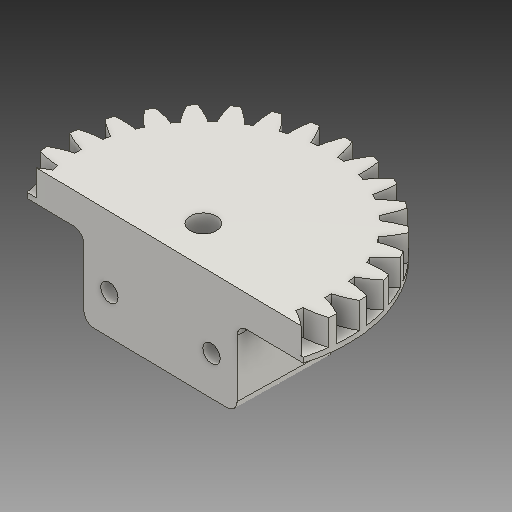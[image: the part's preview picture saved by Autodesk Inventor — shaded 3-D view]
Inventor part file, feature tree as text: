
AUTODESK INVENTOR PART (.ipt)
format: ipt  version: 2018 (Build 220112000, 112)  size: 329,728 bytes
history: native  units: mm
features: other x13, sketch x9, plane x4
ambient origin geometry x8: Origin, YZ Plane, XZ Plane, XY Plane, X Axis, Y Axis, Z Axis, Center Point
bodies: Volumenkörper1 (feature_tree)
feature tree (26):
  other  "Stirnzahnrad1"
  other  "Solid1::Stirnzahnrad1"
  other  "Bezeichnung1"
  sketch  "Sketch1"  dims[d0=10.0mm]
  sketch  "Sketch2"  dims[d16=40.0mm]
  sketch  "Skizze9"  dims[d17=0.0mm]
  sketch  "Skizze10"  dims[d41=0.0mm]
  sketch  "Skizze11"  dims[d43=40.0mm]
  sketch  "Skizze12"  dims[d46=40.0mm]
  sketch  "Skizze13"  dims[d47=0.0mm]
  sketch  "Skizze14"  dims[d48=0.0mm]
  sketch  "Skizze15"
  plane  "XZ Plane_1"
  plane  "Work Plane2"
  plane  "Work Plane8"
  plane  "Work Plane9"
  other  "Z Axis_1"
  other  "Flä1"
  other  "Srf1::Abgeleitet"
  other  "Abstands-iMate"
  other  "Ausrichtungs-iMate"
  other  "Netz-iMate"
  other  "Achsen-iMate"
  other  "Positions-iMate"
  other  "Netz-iMate 2"
  other  "Startebenen-iMate"
